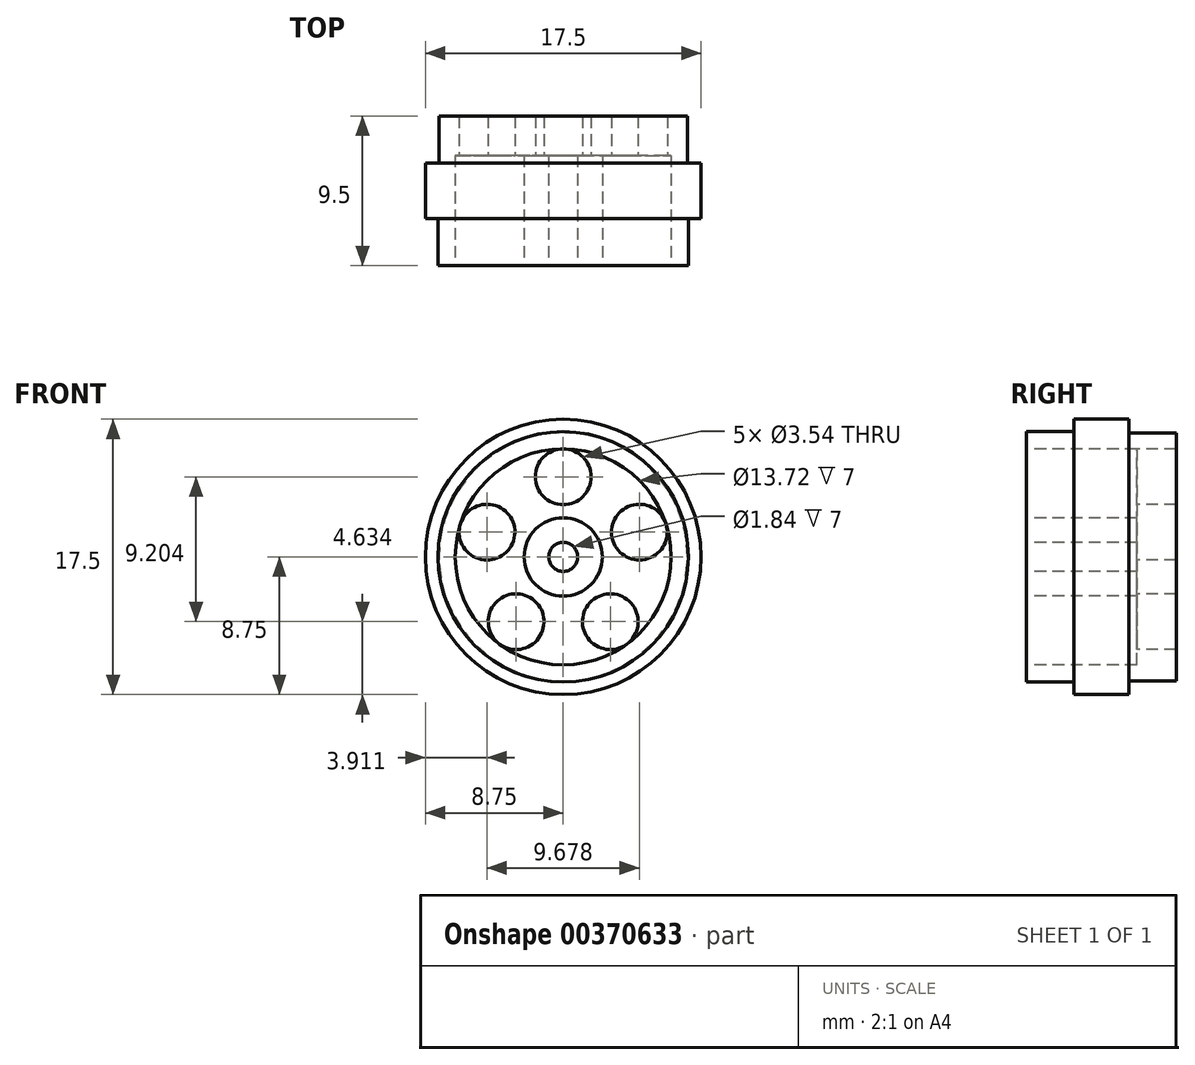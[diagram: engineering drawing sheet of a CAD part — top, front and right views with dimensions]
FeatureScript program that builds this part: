
annotation { "Feature Type Name" : "Feature", "Feature Type Description" : "" }
export const myFeature = defineFeature(function(context is Context, id is Id, definition is map)
    precondition{}
    {
        {
            var Q0;
            Q0=qCreatedBy(makeId("Front.planeOp"),FACE);
            var sketch = newSketch(context, id + "F0", { "sketchPlane" : qUnion([Q0])});
            skCircle(sketch, "E0", {"center": v(0, 0) * mm, "radius": 7.95 * mm});
            skSolve(sketch);
        }
        {
            var Q0;
            Q0=makeQuery(id+"F0.imprint","IMPRINT",FACE,{"disambiguationData":[TD([[makeQuery(id+"F0.imprint","IMPRINT",EDGE,{"derivedFrom":sQuery(id+"F0.wireOp",EDGE,"E0")}),1.0]])]});
            extrude(context, id + "F1", {"entities" : qUnion([Q0]), "depth" : 3 * mm});
        }
        {
            var Q0;
            Q0=makeQuery(id+"F1.opExtrude","CAP_FACE",FACE,{"disambiguationData":[OSD([sQuery(id+"F0.wireOp",EDGE,"E0")])],"isStart":true});
            var sketch = newSketch(context, id + "F2", { "sketchPlane" : qUnion([Q0])});
            skCircle(sketch, "E1", {"center": v(0, 0) * mm, "radius": 8.75 * mm});
            skSolve(sketch);
        }
        {
            var Q0;
            Q0 = qSketchRegion(id + "F2", true);
            extrude(context, id + "F3", {"entities" : qUnion([Q0]), "operationType" : NewBodyOperationType.ADD, "depth" : 3.5 * mm});
        }
        {
            var Q0;
            Q0=makeQuery(id+"F3.opExtrude","CAP_FACE",FACE,{"disambiguationData":[OSD([sQuery(id+"F2.wireOp",EDGE,"E1")])],"isStart":false});
            var sketch = newSketch(context, id + "F4", { "sketchPlane" : qUnion([Q0])});
            skCircle(sketch, "E2", {"center": v(0, 0) * mm, "radius": 7.95 * mm});
            skSolve(sketch);
        }
        {
            var Q0;
            Q0=makeQuery(id+"F4.imprint","IMPRINT",FACE,{"disambiguationData":[TD([[makeQuery(id+"F4.imprint","IMPRINT",EDGE,{"derivedFrom":sQuery(id+"F4.wireOp",EDGE,"E2")}),-1.0]])]});
            var sketch = newSketch(context, id + "F5", { "sketchPlane" : qUnion([Q0])});
            skCircle(sketch, "E3", {"center": v(0, 0) * mm, "radius": 7.88 * mm});
            skSolve(sketch);
        }
        {
            var Q0;
            Q0 = qSketchRegion(id + "F5", true);
            extrude(context, id + "F6", {"entities" : qUnion([Q0]), "operationType" : NewBodyOperationType.ADD, "depth" : 3 * mm});
        }
        {
            var Q0;
            Q0=makeQuery(id+"F1.opExtrude","CAP_FACE",FACE,{"disambiguationData":[OSD([sQuery(id+"F0.wireOp",EDGE,"E0")])],"isStart":false});
            var sketch = newSketch(context, id + "F7", { "sketchPlane" : qUnion([Q0])});
            skCircle(sketch, "E4", {"center": v(0, 5.09) * mm, "radius": 1.77 * mm});
            skCircle(sketch, "E5.1.0", {"center": v(-4.84, 1.57) * mm, "radius": 1.77 * mm});
            skCircle(sketch, "E5.2.0", {"center": v(-3, -4.12) * mm, "radius": 1.77 * mm});
            skCircle(sketch, "E5.3.0", {"center": v(3, -4.12) * mm, "radius": 1.77 * mm});
            skCircle(sketch, "E5.4.0", {"center": v(4.84, 1.57) * mm, "radius": 1.77 * mm});
            skPoint(sketch, "E5.center", {"position": v(0, 0) * mm});
            skSolve(sketch);
        }
        {
            var Q0;
            Q0 = qSketchRegion(id + "F7", true);
            extrude(context, id + "F8", {"entities" : qUnion([Q0]), "operationType" : NewBodyOperationType.REMOVE, "oppositeDirection" : true, "depth" : 25 * mm});
        }
        {
            var Q0;
            Q0=makeQuery(id+"F1.opExtrude","CAP_FACE",FACE,{"disambiguationData":[OSD([sQuery(id+"F0.wireOp",EDGE,"E0")])],"isStart":false});
            var sketch = newSketch(context, id + "F9", { "sketchPlane" : qUnion([Q0])});
            skCircle(sketch, "E6", {"center": v(0, 0) * mm, "radius": 0.92 * mm});
            skCircle(sketch, "E7", {"center": v(0, 0) * mm, "radius": 2.49 * mm});
            skCircle(sketch, "E8", {"center": v(0, 0) * mm, "radius": 6.86 * mm});
            skSolve(sketch);
        }
        {
            var Q0;
            Q0 = qSketchRegion(id + "F9", true);
            var Q1;
            Q1=makeQuery(id+"F9.imprint","IMPRINT",FACE,{"disambiguationData":[TD([[makeQuery(id+"F9.imprint","IMPRINT",EDGE,{"derivedFrom":sQuery(id+"F9.wireOp",EDGE,"E6")}),1.0]])]});
            extrude(context, id + "F10", {"entities" : qUnion([Q0, Q1]), "operationType" : NewBodyOperationType.REMOVE, "oppositeDirection" : true, "depth" : 7 * mm});
        }
    });
